# Revit family: DYNRDHL
name_source: partatom
category: Lighting Fixtures
units: mm (PartAtom-declared; Revit-internal decimal feet)

## family parameters
Cut with Voids When Loaded = No
Host = Face
Light Source = No
OmniClass Number = 23.85.80.11.27
OmniClass Title = Lighting Controls
Part Type = Normal
Room Calculation Point = No
Round Connector Dimension = Use Diameter
Shared = Yes

## types (1)
- DYNRDHL
    Angle = 90.00°
    Apparent Load = 32 VA
    Default Elevation = 48"
    Description = NEMA 4X HIGH LUMEN INDUSTRIAL LED EMERGENCY LIGHT
    Features = High lumen, high mounting height
•  Up to 168’ multi-unit spacing
•  90-minute full lumen output
•  Self-test/self-diagnostics standard
•  Wet and NEMA 4X application
•  Food processing option
•  Remote laser tester option
•  Long-life lithium iron phosphate battery
•  CEC T20 compliant
•  Matching remote heads
    Housing Material = Finish - Gray
    Lamp = LED
    Lens Element = Glass
    Manufacturer = Current Lighting
    Model = DYNRDHL
    Type Comments = Light Fixture
    URL = https://www.currentlighting.com
    Warranty = 5 Years Limited
    Wattage Comments = 32 W
    Width = 10"

## geometry (parser evidence)
native form markers: Blend x2, Sweep x8
no freeform markers — native parametric forms only
